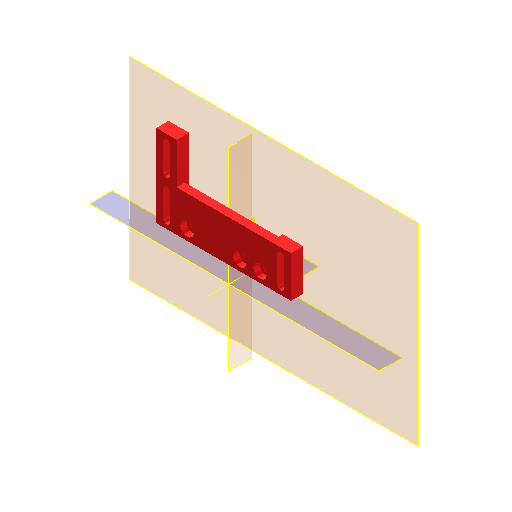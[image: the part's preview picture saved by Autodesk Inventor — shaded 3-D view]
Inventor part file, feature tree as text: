
AUTODESK INVENTOR PART (.ipt)
format: ipt  version: 2025.3 (Build 293356000, 356)  size: 264,704 bytes
history: native  units: mm
features: other x14, reference x11, plane x9, extrude x6, sketch x6, projected_geometry x3, hole x1
ambient origin geometry x8: Origin, YZ Plane, XZ Plane, XY Plane, X Axis, Y Axis, Z Axis, Center Point
bodies: Volumenkörper1 (feature_tree)
feature tree (50):
  plane  "Arbeitsebene1"
  plane  "Arbeitsebene2"
  extrude  "Extrusion1"  Depth=6.0mm
  hole  "Bohrung1"  [1 undecoded]
  sketch  "Skizze3"  dims[d2=2.9mm d3=6.0mm d4=6.5mm d5=3.0mm d6=90.0deg d7=8.0mm d8=20.594885mm d9=38.0mm]
  other  "Arbeitspunkt1"
  plane  "Arbeitsebene4"
  plane  "Arbeitsebene5"
  extrude  "Extrusion2"  Depth=10.0mm
  plane  "Arbeitsebene3"
  other  "Arbeitsachse1"
  plane  "Arbeitsebene8"
  extrude  "Extrusion5"  Depth=10.0mm
  extrude  "Extrusion6"  Depth=10.0mm
  extrude  "Extrusion7"  Depth=10.0mm
  sketch  "Sketch11"  dims[d31=10.0mm d32=10.0mm d33=10.0mm d34=6.5mm d35=3.2mm d36=6.5mm d37=3.2mm d47=11.8mm d49=20.0mm d50=6.5mm d51=3.2mm d54=0.1mm d55=12.5mm d56=0.0mm d57=5.0mm d58=0.0mm d59=0.0mm d60=10.0mm d61=0.0mm d62=10.0mm d63=0.0mm]
  plane  "Work Plane9"
  extrude  "Extrusion8"  Depth=10.0mm
  reference  "Referenz1"
  reference  "Referenz3"
  reference  "Referenz4"
  sketch  "Skizze2"  dims[d0=10.0mm d1=0.0mm]
  reference  "Referenz5"
  reference  "Referenz6"
  reference  "Referenz7"
  projected_geometry  "Projizierte Kontur1"
  reference  "Referenz8"
  reference  "Referenz9"
  plane  "Arbeitsebene6"
  plane  "Arbeitsebene7"
  sketch  "Skizze8"  dims[d10=10.0mm d11=10.0mm]
  reference  "Referenz18"
  sketch  "Skizze9"  dims[d12=10.0mm d13=10.0mm]
  projected_geometry  "Projizierte Kontur3"
  sketch  "Sketch10"  dims[d14=6.0mm d15=0.0mm d30=10.0mm]
  reference  "Reference19"
  reference  "Reference20"
  projected_geometry  "Projected Loop4"
  other  "Assemlby_Scanner_v1.iam"
  other  "00_CCTV_lens_M12_25mm_5mp:1"
  other  "Assemlby_lightsheet_generator_passive_v2.iam"
  other  "30_Lightsheet_generator_passive_lid_v0:1"
  other  "00_Thorlabs_LJ1878L1-A-Step:1"
  other  "<userpath>\Documents\HoLiSheet\INVENTOR\Assemlby_lightsheet_generator_passive_v2.iam"
  other  "30_Lightsheet_generator_singlegalvo_1:1"
  other  "30_Scanlens_Laseradaper_v1:1"
  other  "Assembly_Guinardia_V2.iam"
  other  "10_Wellplate_base_v2:1"
  other  "Assembly_Guinardia_V4.iam"
  other  "10_Wellplate_base_v3:1"
note: 1 required parameter value undecoded (feature->parameter linkage not recoverable at this tier; creation-order binding heuristic only, values carry confidence <= 0.55)
